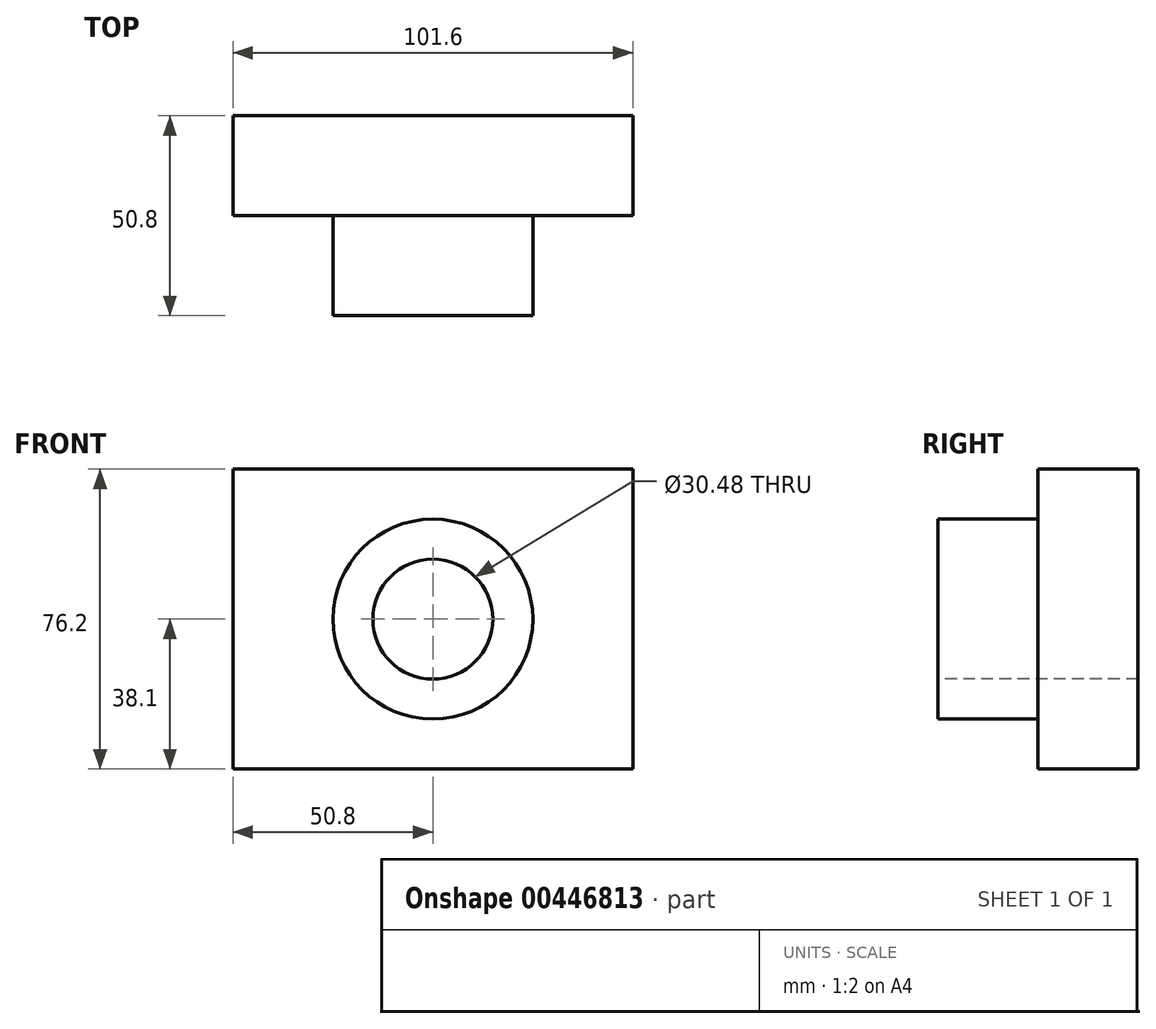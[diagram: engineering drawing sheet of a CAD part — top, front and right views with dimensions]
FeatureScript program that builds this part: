
annotation { "Feature Type Name" : "Feature", "Feature Type Description" : "" }
export const myFeature = defineFeature(function(context is Context, id is Id, definition is map)
    precondition{}
    {
        {
            var Q0;
            Q0=qCreatedBy(makeId("Front.planeOp"),FACE);
            var sketch = newSketch(context, id + "F0", { "sketchPlane" : qUnion([Q0])});
            skLineSegment(sketch, "E0.bottom", {"start": v(-50.8, 38.1) * mm, "end": v(50.8, 38.1) * mm});
            skLineSegment(sketch, "E0.top", {"start": v(-50.8, -38.1) * mm, "end": v(50.8, -38.1) * mm});
            skLineSegment(sketch, "E0.left", {"start": v(-50.8, 38.1) * mm, "end": v(-50.8, -38.1) * mm});
            skLineSegment(sketch, "E0.right", {"start": v(50.8, 38.1) * mm, "end": v(50.8, -38.1) * mm});
            skSolve(sketch);
        }
        {
            var Q0;
            Q0 = qSketchRegion(id + "F0", true);
            extrude(context, id + "F1", {"entities" : qUnion([Q0]), "depth" : 25.4 * mm});
        }
        {
            var Q0;
            Q0=makeQuery(id+"F1.opExtrude","CAP_FACE",FACE,{"disambiguationData":[OSD([sQuery(id+"F0.wireOp",EDGE,"E0.bottom"),sQuery(id+"F0.wireOp",EDGE,"E0.top"),sQuery(id+"F0.wireOp",EDGE,"E0.left"),sQuery(id+"F0.wireOp",EDGE,"E0.right")])],"isStart":false});
            var sketch = newSketch(context, id + "F2", { "sketchPlane" : qUnion([Q0])});
            skCircle(sketch, "E1", {"center": v(0, 0) * mm, "radius": 25.4 * mm});
            skSolve(sketch);
        }
        {
            var Q0;
            Q0 = qSketchRegion(id + "F2", true);
            extrude(context, id + "F3", {"entities" : qUnion([Q0]), "operationType" : NewBodyOperationType.ADD, "depth" : 25.4 * mm});
        }
        {
            var Q0;
            Q0=makeQuery(id+"F3.opExtrude","CAP_FACE",FACE,{"disambiguationData":[OSD([sQuery(id+"F2.wireOp",EDGE,"E1")])],"isStart":false});
            var sketch = newSketch(context, id + "F4", { "sketchPlane" : qUnion([Q0])});
            skCircle(sketch, "E2", {"center": v(0, 0) * mm, "radius": 15.24 * mm});
            skSolve(sketch);
        }
        {
            var Q0;
            Q0 = qSketchRegion(id + "F4", true);
            extrude(context, id + "F5", {"entities" : qUnion([Q0]), "operationType" : NewBodyOperationType.REMOVE, "oppositeDirection" : true, "depth" : 61.72 * mm});
        }
    });
